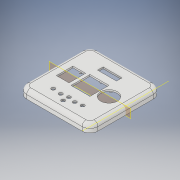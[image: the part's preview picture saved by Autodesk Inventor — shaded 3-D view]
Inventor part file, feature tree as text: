
AUTODESK INVENTOR PART (.ipt)
format: ipt  version: 2017 (Build 210142000, 142)  size: 308,224 bytes
history: native  units: in
note: dims shown in document units (in); Inventor stores cm internally (conversion verified against a paired STEP export)
features: reference x31, sketch x10, extrude x9, other x8, projected_geometry x2, shell x1, fillet x1
ambient origin geometry x8: Origin, YZ Plane, XZ Plane, XY Plane, X Axis, Y Axis, Z Axis, Center Point
bodies: Solid1 (feature_tree)
feature tree (62):
  extrude  "Extrusion1"  Depth=3.5433in
  other  "Work Axis1"
  shell  "Shell2"  Thickness=0.3937in
  fillet  "Fillet1"  Radius=0.0787in
  extrude  "Extrusion2"  Depth=0.3937in
  extrude  "Extrusion3"  Depth=0.0197in
  extrude  "Extrusion4"  Depth=0.0197in
  extrude  "Extrusion5"  Depth=0.1575in
  extrude  "Extrusion6"  Depth=0.1575in
  extrude  "Extrusion7"  Depth=0.059in TaperAngle=0.0deg
  sketch  "Sketch8"  dims[d25=0.039in d26=0.0in d27=0.098in d28=0.0in]
  extrude  "Extrusion8"  Depth=0.098in TaperAngle=0.0deg
  extrude  "Extrusion9"  Depth=0.059in TaperAngle=0.0deg
  sketch  "Sketch1"  dims[d0=3.5433in d1=3.5433in d2=0.3937in d3=0.0in d5=0.0787in]
  sketch  "Sketch2"  dims[d6=0.1969in d10=0.3937in]
  reference  "Reference1"
  reference  "Reference2"
  reference  "Reference3"
  reference  "Reference4"
  reference  "Reference5"
  reference  "Reference6"
  reference  "Reference7"
  reference  "Reference8"
  reference  "Reference9"
  reference  "Reference10"
  sketch  "Sketch3"  dims[d13=0.0197in d14=0.0197in]
  reference  "Reference11"
  reference  "Reference12"
  reference  "Reference13"
  reference  "Reference14"
  reference  "Reference15"
  reference  "Reference16"
  reference  "Reference17"
  sketch  "Sketch4"  dims[d15=0.0197in d16=0.0197in]
  sketch  "Sketch5"  dims[d17=0.0in d18=0.0in d19=0.1575in]
  sketch  "Sketch6"  dims[d20=0.1575in d21=0.1575in]
  reference  "Reference18"
  reference  "Reference19"
  sketch  "Sketch7"  dims[d22=0.1063in d23=0.059in d24=0.0in]
  projected_geometry  "Projected Loop1"
  projected_geometry  "Projected Loop2"
  sketch  "Sketch9"  dims[d29=0.1181in d30=0.059in d31=0.0in]
  reference  "Reference20"
  reference  "Reference21"
  reference  "Reference22"
  reference  "Reference23"
  reference  "Reference24"
  reference  "Reference25"
  sketch  "Sketch10"  dims[d32=0.1181in d33=0.0197in d34=0.0591in d35=0.0394in d36=0.1575in d37=0.0in d38=3.1102in d39=0.0197in d40=0.0in d41=0.0in d42=0.1575in d43=0.0591in d44=0.1181in d45=0.0in]
  reference  "Reference26"
  reference  "Reference27"
  reference  "Reference28"
  reference  "Reference29"
  reference  "Reference30"
  reference  "Reference31"
  parser-record x1  (decoder bookkeeping rows leaked as tree rows — omitted from the tree; the rows remain in map.json)
  other  "Body_as.iam"
  other  "CO2_Sensor:1"
  other  "MotionSensor:1"
  other  "DHT22:1"
  other  "OLED_128x32:1"
  other  "Keyboard1:1"
note: 1 file-system path scrubbed to <path> (originals preserved in map.json)
